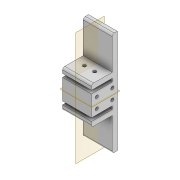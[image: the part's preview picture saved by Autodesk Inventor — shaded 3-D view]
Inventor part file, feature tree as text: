
AUTODESK INVENTOR PART (.ipt)
format: ipt  version: 2022 (Build 260153000, 153)  size: 174,592 bytes
history: native  units: mm
features: extrude x4, sketch x4, plane x2, projected_geometry x2, fillet x1
ambient origin geometry x8: Origin, YZ Plane, XZ Plane, XY Plane, X Axis, Y Axis, Z Axis, Center Point
bodies: Solid1 (feature_tree)
feature tree (13):
  extrude  "Extrusion1"  Depth=100.0mm
  extrude  "Extrusion2"  Depth=5.0mm
  extrude  "Extrusion3"  Depth=10.0mm
  plane  "Work Plane1"
  extrude  "Extrusion11"  Depth=5.0mm
  fillet  "Fillet1"  Radius=3.1mm
  plane  "Work Plane3"
  sketch  "Sketch1"  dims[d0=28.0mm d1=100.0mm]
  sketch  "Sketch3"  dims[d2=5.0mm d3=0.0mm d6=50.0mm]
  projected_geometry  "Projected Loop2"
  sketch  "Sketch4"  dims[d7=100.0mm d8=10.0mm]
  projected_geometry  "Projected Loop3"
  sketch  "Sketch13"  dims[d9=10.0mm d10=5.0mm d11=3.1mm d12=3.1mm d13=5.0mm d14=20.0mm d15=0.0mm d16=3.1mm d17=3.1mm d18=4.95mm d19=4.95mm d20=8.0mm d21=8.0mm d22=100.0mm d23=0.0mm d57=3.0mm d58=3.0mm d59=3.0mm d60=3.0mm d61=5.0mm d62=5.0mm d63=5.0mm d64=5.0mm d65=5.0mm d67=5.0mm d69=5.0mm d70=5.0mm d71=180.0mm d72=0.0mm d73=2.0mm]
